# Revit family: Loading-Dock-Equipment_Leveler_Poweramp_CA6820
name_source: partatom
category: Generic Models
units: mm (PartAtom-declared; Revit-internal decimal feet)

## family parameters
Always vertical = Yes
Can host rebar = No
Cut with Voids When Loaded = Yes
Maintain Annotation Orientation = No
Part Type = Normal
Room Calculation Point = No
Round Connector Dimension = Use Diameter
Shared = No
Work Plane-Based = Yes

## types (1)
- Loading-Dock-Equipment_Leveler_Poweramp_CA6820
    Default Elevation = 48"
    Dimensions (L x W x H) = 81 1/2 x 72 x 19
    Height = 19"
    Length = 81 1/2"
    Load = 0 VA
    Manufacturer = POWERAMP
    Model = CA6820
    Poles = 1
    Product Documentation Link = https://www.poweramp.com
    Product Page URL = https://www.arcat.com
    Specification = https://www.poweramp.com
    URL = https://www.poweramp.com
    Voltage = 0 V
    Width = 72"

## geometry (parser evidence)
native form markers: Sweep x9
no freeform markers — native parametric forms only
